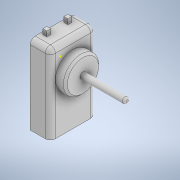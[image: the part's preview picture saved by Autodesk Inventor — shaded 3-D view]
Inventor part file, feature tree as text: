
AUTODESK INVENTOR PART (.ipt)
format: ipt  version: 2022 (Build 260153070, 153G)  size: 163,840 bytes
history: native  units: mm
features: sketch x5, extrude x4, fillet x3, chamfer x1
ambient origin geometry x8: Origin, YZ Plane, XZ Plane, XY Plane, X Axis, Y Axis, Z Axis, Center Point
bodies: Solid1 (feature_tree)
feature tree (13):
  extrude  "Extrusion1"  Depth=45.0mm
  extrude  "Extrusion2"  Depth=35.0mm
  extrude  "Extrusion3"  Depth=10.0mm
  fillet  "Fillet1"  Radius=10.0mm
  extrude  "Extrusion4"  Depth=44.0mm TaperAngle=0.0deg
  chamfer  "Chamfer1"  Distance=4.0mm
  fillet  "Fillet2"  Radius=4.0mm
  fillet  "Fillet3"  Radius=4.0mm
  sketch  "Sketch5"  dims[d12=5.0mm d13=4.0mm d14=4.0mm d15=4.0mm d16=4.0mm d17=5.0mm d18=9.0mm d19=5.0mm d20=0.0mm d21=2.0mm d22=2.0mm d23=45.0deg d24=5.0mm d25=2.0mm]
  sketch  "Sketch1"  dims[d0=78.6mm d1=45.0mm]
  sketch  "Sketch2"  dims[d2=20.0mm d3=0.0mm d4=35.0mm]
  sketch  "Sketch3"  dims[d5=22.5mm d6=50.8mm d7=10.0mm d8=0.0mm]
  sketch  "Sketch4"  dims[d9=6.0mm d10=44.0mm d11=0.0mm]
